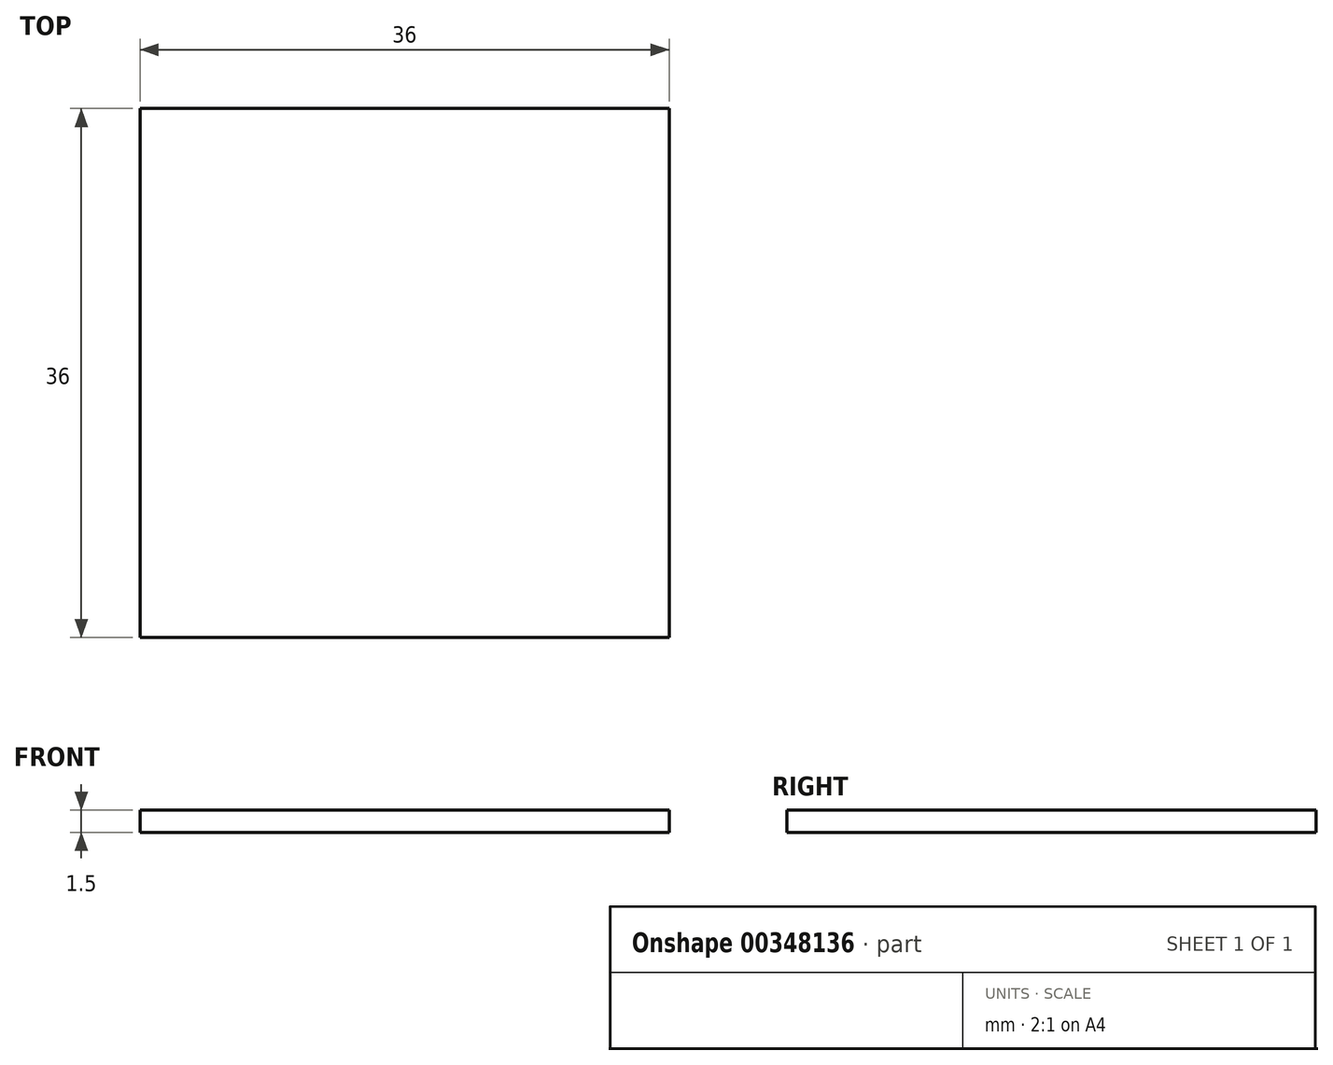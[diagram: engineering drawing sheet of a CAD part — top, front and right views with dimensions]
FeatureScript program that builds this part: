
annotation { "Feature Type Name" : "Feature", "Feature Type Description" : "" }
export const myFeature = defineFeature(function(context is Context, id is Id, definition is map)
    precondition{}
    {
        {
            var Q0;
            Q0=qCreatedBy(makeId("Top.planeOp"),FACE);
            var sketch = newSketch(context, id + "F0", { "sketchPlane" : qUnion([Q0])});
            skLineSegment(sketch, "E0.bottom", {"start": v(18, 18) * mm, "end": v(-18, 18) * mm});
            skLineSegment(sketch, "E0.top", {"start": v(18, -18) * mm, "end": v(-18, -18) * mm});
            skLineSegment(sketch, "E0.left", {"start": v(18, 18) * mm, "end": v(18, -18) * mm});
            skLineSegment(sketch, "E0.right", {"start": v(-18, 18) * mm, "end": v(-18, -18) * mm});
            skPoint(sketch, "E0.middle", {"position": v(0, 0) * mm});
            skSolve(sketch);
        }
        {
            var Q0;
            Q0=makeQuery(id+"F0.imprint","IMPRINT",FACE,{"disambiguationData":[TD([[makeQuery(id+"F0.imprint","IMPRINT",EDGE,{"derivedFrom":sQuery(id+"F0.wireOp",EDGE,"E0.bottom")}),1.0]])]});
            extrude(context, id + "F1", {"entities" : qUnion([Q0]), "depth" : 1.5 * mm});
        }
    });
